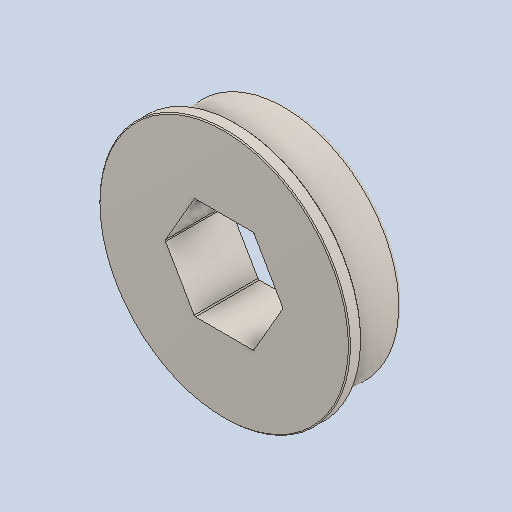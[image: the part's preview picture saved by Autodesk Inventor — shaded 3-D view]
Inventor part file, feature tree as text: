
AUTODESK INVENTOR PART (.ipt)
format: ipt  version: 2023 (Build 270158000, 158)  size: 154,624 bytes
history: native  units: in
note: dims shown in document units (in); Inventor stores cm internally (conversion verified against a paired STEP export)
features: fillet x1
ambient origin geometry x8: Origin, YZ Plane, XZ Plane, XY Plane, X Axis, Y Axis, Z Axis, Center Point
bodies: Solid1 (feature_tree)
feature tree (1):
  fillet  "Fillet2"  [1 undecoded]
note: 1 required parameter value undecoded (feature->parameter linkage not recoverable at this tier; creation-order binding heuristic only, values carry confidence <= 0.55)
